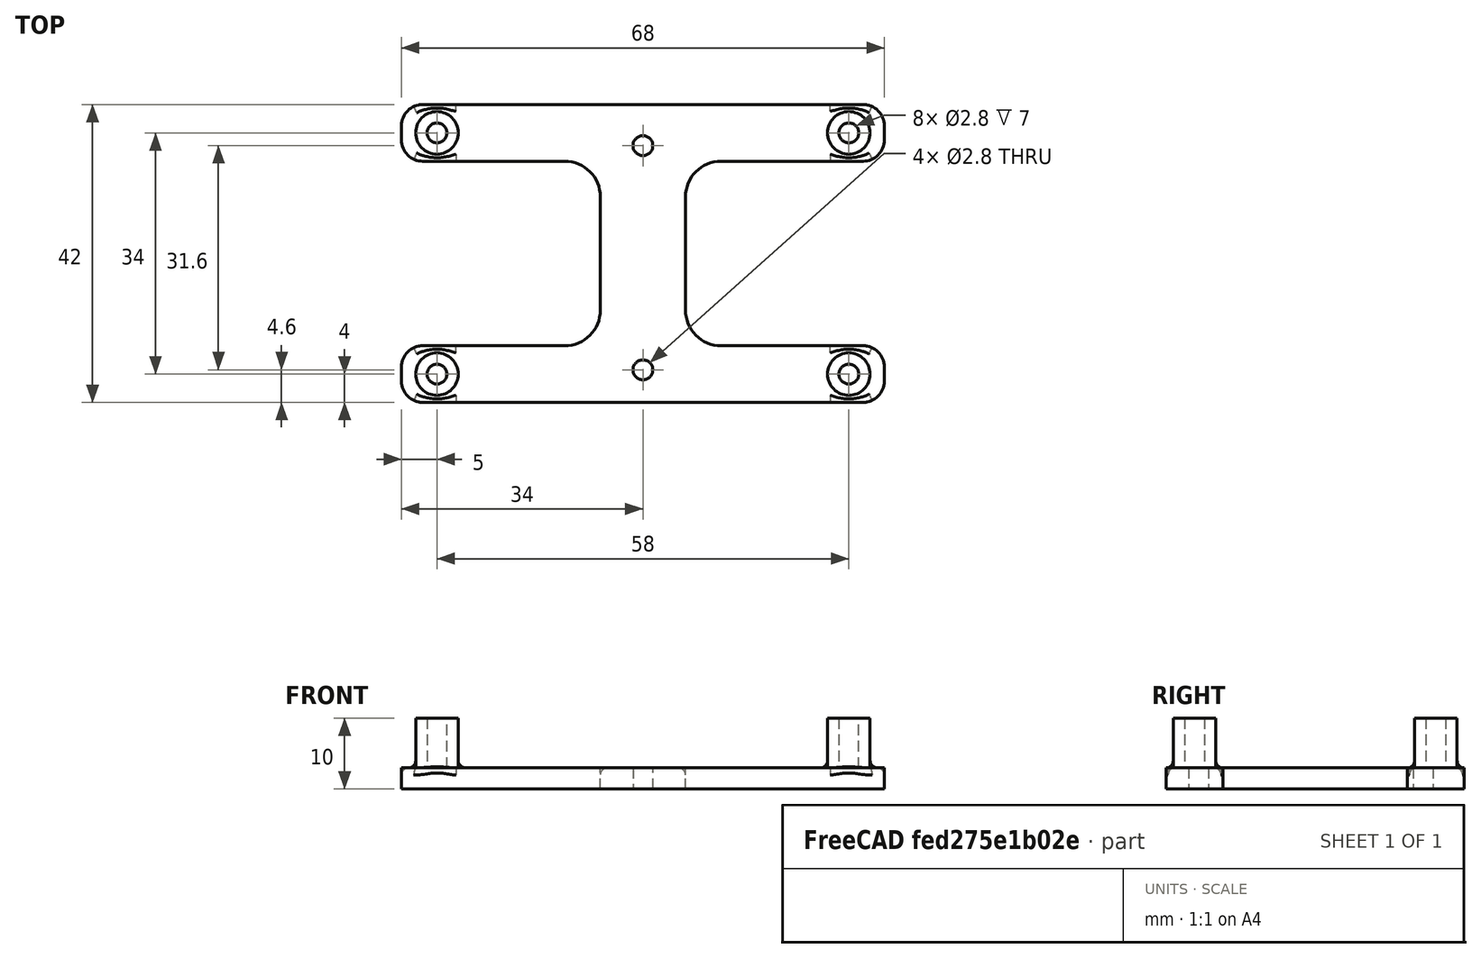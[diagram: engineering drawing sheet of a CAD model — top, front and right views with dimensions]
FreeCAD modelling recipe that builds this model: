
FCSTD DOCUMENT  (FreeCAD 0.19R24291 (Git))
Label: Nanopi M1 Din Rail Mount
License: All rights reserved
LicenseURL: http://en.wikipedia.org/wiki/All_rights_reserved
objects: Sketcher::SketchObject×2, PartDesign::Pad×2, Part::Fillet×2, Mesh::Feature×1, PartDesign::Body×1, Part::Feature×1
note: 10 computed .brp shape members not serialized (recipe doc carries the construction recipe); baked Part::Feature solids carry a one-line shape summary decoded from their .brp

FEATURE [Mesh::Feature] pcb_din_clip_x3
  Placement = pos=(5,-150,-159) rot=(0,-1,0;1.5708rad)
FEATURE [Sketcher::SketchObject] Sketch
  FullyConstrained = true
  MapMode = 5
  Support = -> [XY_Plane]
  sketch-geometry (30):
    g0: LineSegment StartX=-34 StartY=30 StartZ=0 EndX=34 EndY=30 EndZ=0
    g1: LineSegment StartX=34 StartY=30 StartZ=0 EndX=34 EndY=-30 EndZ=0
    g2: LineSegment StartX=34 StartY=-30 StartZ=0 EndX=-34 EndY=-30 EndZ=0
    g3: LineSegment StartX=-34 StartY=-30 StartZ=0 EndX=-34 EndY=30 EndZ=0
    g4: LineSegment StartX=-31 StartY=30 StartZ=0 EndX=31 EndY=30 EndZ=0
    g5: LineSegment StartX=-34 StartY=27 StartZ=0 EndX=-34 EndY=25 EndZ=0
    g6: LineSegment StartX=-31 StartY=22 StartZ=0 EndX=-11 EndY=22 EndZ=0
    g7: LineSegment StartX=-6 StartY=17 StartZ=0 EndX=-6 EndY=1 EndZ=0
    g8: LineSegment StartX=-11 StartY=-4 StartZ=0 EndX=-31 EndY=-4 EndZ=0
    g9: LineSegment StartX=-34 StartY=-7 StartZ=0 EndX=-34 EndY=-9 EndZ=0
    g10: LineSegment StartX=-31 StartY=-12 StartZ=0 EndX=31 EndY=-12 EndZ=0
    g11: LineSegment StartX=34 StartY=-9 StartZ=0 EndX=34 EndY=-7 EndZ=0
    g12: LineSegment StartX=31 StartY=-4 StartZ=0 EndX=11 EndY=-4 EndZ=0
    g13: LineSegment StartX=6 StartY=1 StartZ=0 EndX=6 EndY=17 EndZ=0
    g14: LineSegment StartX=11 StartY=22 StartZ=0 EndX=31 EndY=22 EndZ=0
    g15: LineSegment StartX=34 StartY=25 StartZ=0 EndX=34 EndY=27 EndZ=0
    g16: ArcOfCircle CenterX=-31 CenterY=27 CenterZ=0 NormalX=0 NormalY=0 NormalZ=1 AngleXU=0 Radius=3 StartAngle=1.5708 EndAngle=3.14159
    g17: ArcOfCircle CenterX=-31 CenterY=25 CenterZ=0 NormalX=0 NormalY=0 NormalZ=1 AngleXU=0 Radius=3 StartAngle=3.14159 EndAngle=4.71239
    g18: ArcOfCircle CenterX=31 CenterY=25 CenterZ=0 NormalX=0 NormalY=0 NormalZ=1 AngleXU=0 Radius=3 StartAngle=4.71239 EndAngle=6.28319
    g19: ArcOfCircle CenterX=31 CenterY=27 CenterZ=0 NormalX=0 NormalY=0 NormalZ=1 AngleXU=0 Radius=3 StartAngle=0 EndAngle=1.5708
    g20: ArcOfCircle CenterX=31 CenterY=-7 CenterZ=0 NormalX=0 NormalY=0 NormalZ=1 AngleXU=0 Radius=3 StartAngle=0 EndAngle=1.5708
    g21: ArcOfCircle CenterX=31 CenterY=-9 CenterZ=0 NormalX=0 NormalY=0 NormalZ=1 AngleXU=0 Radius=3 StartAngle=4.71239 EndAngle=6.28319
    g22: ArcOfCircle CenterX=-31 CenterY=-9 CenterZ=0 NormalX=0 NormalY=0 NormalZ=1 AngleXU=0 Radius=3 StartAngle=3.14159 EndAngle=4.71239
    g23: ArcOfCircle CenterX=-31 CenterY=-7 CenterZ=0 NormalX=0 NormalY=0 NormalZ=1 AngleXU=0 Radius=3 StartAngle=1.5708 EndAngle=3.14159
    g24: ArcOfCircle CenterX=-11 CenterY=17 CenterZ=0 NormalX=0 NormalY=0 NormalZ=1 AngleXU=0 Radius=5 StartAngle=0 EndAngle=1.5708
    g25: ArcOfCircle CenterX=-11 CenterY=1 CenterZ=0 NormalX=0 NormalY=0 NormalZ=1 AngleXU=0 Radius=5 StartAngle=4.71239 EndAngle=6.28319
    g26: ArcOfCircle CenterX=11 CenterY=1 CenterZ=0 NormalX=0 NormalY=0 NormalZ=1 AngleXU=0 Radius=5 StartAngle=3.14159 EndAngle=4.71239
    g27: ArcOfCircle CenterX=11 CenterY=17 CenterZ=0 NormalX=0 NormalY=0 NormalZ=1 AngleXU=0 Radius=5 StartAngle=1.5708 EndAngle=3.14159
    g28: Circle CenterX=0 CenterY=24.2 CenterZ=0 NormalX=0 NormalY=0 NormalZ=1 AngleXU=0 Radius=1.4
    g29: Circle CenterX=0 CenterY=-7.4 CenterZ=0 NormalX=0 NormalY=0 NormalZ=1 AngleXU=0 Radius=1.4
  constraints (74):
    c: Coincident(g0,g1)
    c: Coincident(g1,g2)
    c: Coincident(g2,g3)
    c: Coincident(g3,g0)
    c: Horizontal(g0)
    c: Horizontal(g2)
    c: Vertical(g1)
    c: Vertical(g3)
    c: DistanceX(g0,g0) = 68
    c: DistanceY(g3,g3) = 60
    c: Symmetric(g2,g0,g-1)
    c: Horizontal(g6)
    c: Vertical(g7)
    c: Horizontal(g8)
    c: Horizontal(g12)
    c: Vertical(g13)
    c: Horizontal(g14)
    c: Tangent(g5,g16) = -1.5708
    c: Tangent(g4,g16) = 1.5708
    c: Tangent(g5,g17) = -1.5708
    c: Tangent(g6,g17) = -1.5708
    c: Tangent(g14,g18) = -1.5708
    c: Tangent(g15,g18) = -1.5708
    c: Tangent(g15,g19) = -1.5708
    c: Tangent(g4,g19) = 1.5708
    c: Tangent(g12,g20) = -1.5708
    c: Tangent(g11,g20) = -1.5708
    c: Tangent(g11,g21) = -1.5708
    c: Tangent(g10,g21) = -1.5708
    c: Tangent(g10,g22) = -1.5708
    c: Tangent(g9,g22) = -1.5708
    c: Tangent(g9,g23) = -1.5708
    c: Tangent(g8,g23) = -1.5708
    c: Tangent(g6,g24) = 1.5708
    c: Tangent(g7,g24) = 1.5708
    c: Tangent(g8,g25) = 1.5708
    c: Tangent(g7,g25) = 1.5708
    c: Tangent(g13,g26) = 1.5708
    c: Tangent(g12,g26) = 1.5708
    c: Tangent(g13,g27) = 1.5708
    c: Tangent(g14,g27) = 1.5708
    c: Equal(g24,g27)
    c: Equal(g27,g25)
    c: Equal(g25,g26)
    c: Radius(g24) = 5
    c: PointOnObject(g5,g3)
    c: DistanceY(g6,g4) = 8
    c: PointOnObject(g15,g1)
    c: PointOnObject(g4,g0)
    c: PointOnObject(g4,g0)
    c: PointOnObject(g15,g1)
    c: PointOnObject(g5,g3)
    c: Tangent(g9,g3)
    c: Tangent(g11,g1)
    c: DistanceY(g10,g8) = 8
    c: Radius(g16) = 3
    c: Equal(g16,g17)
    c: Equal(g17,g19)
    c: Equal(g19,g18)
    c: Equal(g18,g23)
    c: Equal(g23,g22)
    c: Equal(g22,g20)
    c: Equal(g20,g21)
    c: Horizontal(g8,g12)
    c: DistanceX(g7,g13) = 12
    c: Symmetric(g7,g13,g-2)
    c: PointOnObject(g28,g-2)
    c: PointOnObject(g29,g-2)
    c: Radius(g28) = 1.4
    c: Equal(g28,g29)
    c: DistanceY(g29,g-1) = 7.4
    c: DistanceY(g-1,g28) = 24.2
    c: Vertical(g10,g12)
    c: DistanceY(g8,g4) = 34
FEATURE [PartDesign::Pad] Pad
  Direction = (1,1,1)
  Length = 3
  Length2 = 100
  Profile = -> Sketch
  Type = 0
FEATURE [Sketcher::SketchObject] Sketch001
  ExternalGeometry = -> [Pad]
  FullyConstrained = true
  MapMode = 5
  Placement = pos=(0,0,3) rot=(0,0,1;0rad)
  Support = -> [Pad]
  sketch-geometry (11):
    g0: Circle CenterX=-29 CenterY=26 CenterZ=0 NormalX=0 NormalY=0 NormalZ=1 AngleXU=0 Radius=3
    g1: Circle CenterX=-29 CenterY=26 CenterZ=0 NormalX=0 NormalY=0 NormalZ=1 AngleXU=0 Radius=1.4
    g2: Circle CenterX=29 CenterY=26 CenterZ=0 NormalX=0 NormalY=0 NormalZ=1 AngleXU=0 Radius=1.4
    g3: Circle CenterX=29 CenterY=26 CenterZ=0 NormalX=0 NormalY=0 NormalZ=1 AngleXU=0 Radius=3
    g4: LineSegment StartX=-29 StartY=26 StartZ=0 EndX=29 EndY=26 EndZ=0
    g5: Circle CenterX=-29 CenterY=-8 CenterZ=0 NormalX=0 NormalY=0 NormalZ=1 AngleXU=0 Radius=1.4
    g6: Circle CenterX=-29 CenterY=-8 CenterZ=0 NormalX=0 NormalY=0 NormalZ=1 AngleXU=0 Radius=3
    g7: LineSegment StartX=-29 StartY=26 StartZ=0 EndX=-29 EndY=-8 EndZ=0
    g8: Circle CenterX=29 CenterY=-8 CenterZ=0 NormalX=0 NormalY=0 NormalZ=1 AngleXU=0 Radius=1.4
    g9: Circle CenterX=29 CenterY=-8 CenterZ=0 NormalX=0 NormalY=0 NormalZ=1 AngleXU=0 Radius=3
    g10: LineSegment StartX=-29 StartY=-8 StartZ=0 EndX=29 EndY=-8 EndZ=0
  constraints (26):
    c: Coincident(g1,g0)
    c: Radius(g1) = 1.4
    c: Radius(g0) = 3
    c: Coincident(g2,g3)
    c: Radius(g2) = 1.4
    c: Radius(g3) = 3
    c: Coincident(g1,g4)
    c: Coincident(g2,g4)
    c: Distance(g4) = 58
    c: Angle(g4) = 0
    c: Coincident(g5,g6)
    c: Radius(g5) = 1.4
    c: Radius(g6) = 3
    c: Coincident(g1,g7)
    c: Coincident(g5,g7)
    c: Distance(g7) = 34
    c: Perpendicular(g7,g4)
    c: Coincident(g8,g9)
    c: Radius(g8) = 1.4
    c: Radius(g9) = 3
    c: Coincident(g5,g10)
    c: Coincident(g8,g10)
    c: Equal(g4,g10)
    c: Parallel(g10,g4)
    c: DistanceY(g0,g-3) = 4
    c: DistanceX(g-3,g0) = 2
FEATURE [PartDesign::Pad] Pad001
  BaseFeature = -> Pad
  Direction = (1,1,1)
  Length = 7
  Length2 = 100
  Profile = -> Sketch001
  Type = 0
FEATURE [PartDesign::Body] Body
  Group = -> [Sketch,Pad,Sketch001,Pad001]
  Origin = -> Origin
  Tip = -> Pad001
FEATURE [Part::Fillet] Fillet
  Base = -> Pad001
  Edges = 4 edges r=1: [Edge55,Edge57,Edge58,Edge60]
FEATURE [Part::Fillet] Fillet001
  Base = -> Fillet
  Edges = 1 edges r=1: [Edge30]
FEATURE [Part::Feature] Fillet001001
  shape: bbox 68.49 x 44.2 x 10 mm, 96 faces (baked)
